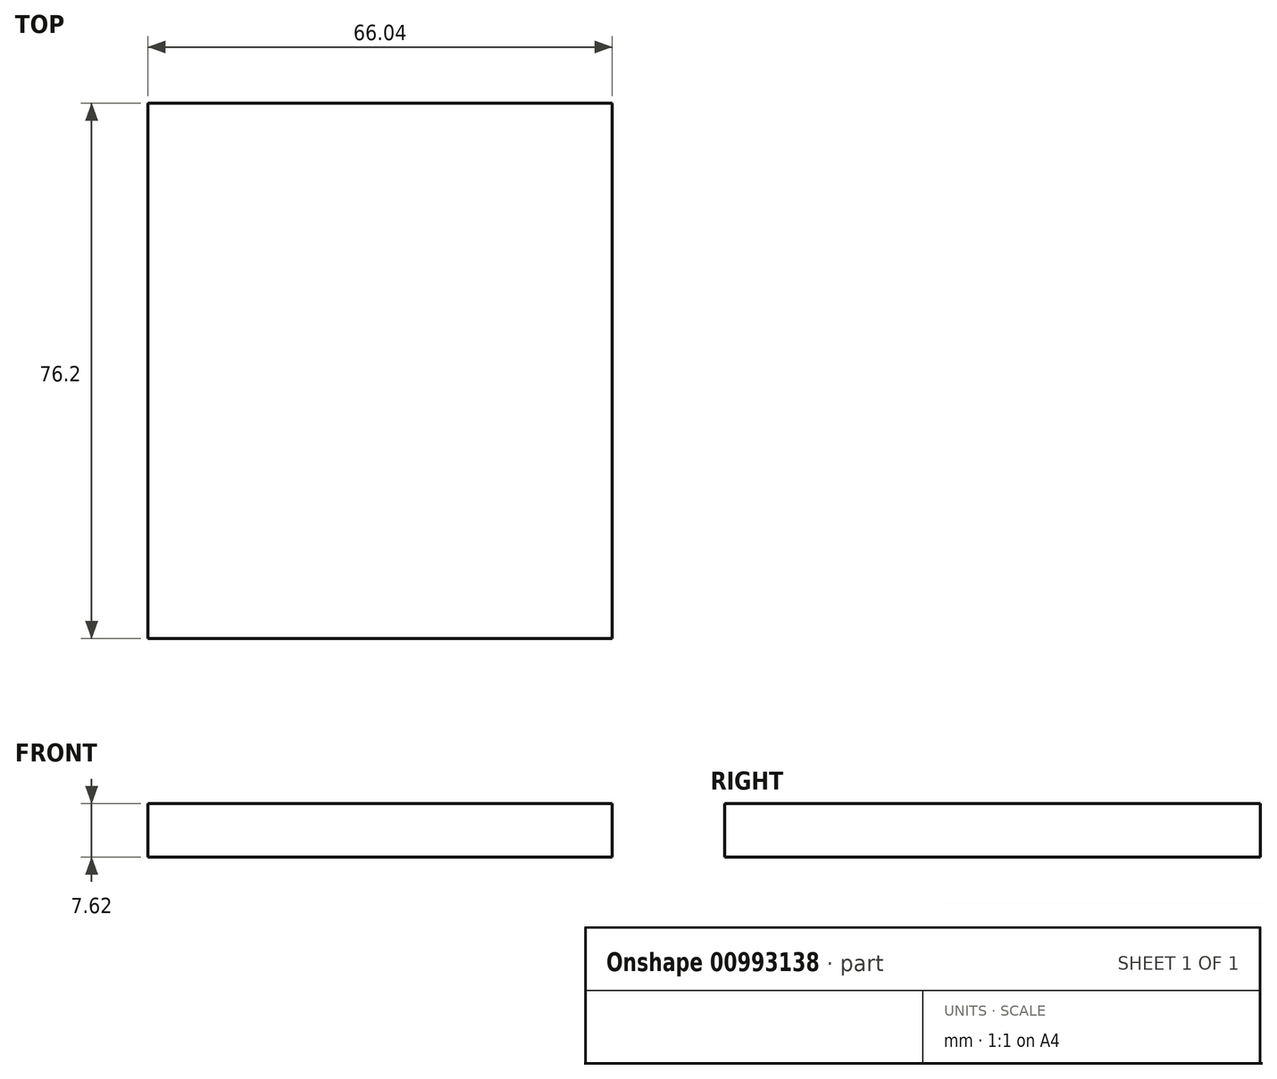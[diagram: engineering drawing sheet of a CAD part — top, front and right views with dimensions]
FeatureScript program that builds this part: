
annotation { "Feature Type Name" : "Feature", "Feature Type Description" : "" }
export const myFeature = defineFeature(function(context is Context, id is Id, definition is map)
    precondition{}
    {
        {
            var Q0;
            Q0=qCreatedBy(makeId("Top.planeOp"),FACE);
            var sketch = newSketch(context, id + "F0", { "sketchPlane" : qUnion([Q0])});
            skLineSegment(sketch, "E0.bottom", {"start": v(-56.06, -63.95) * mm, "end": v(9.98, -63.95) * mm});
            skLineSegment(sketch, "E0.top", {"start": v(-56.06, 12.25) * mm, "end": v(9.98, 12.25) * mm});
            skLineSegment(sketch, "E0.left", {"start": v(-56.06, -63.95) * mm, "end": v(-56.06, 12.25) * mm});
            skLineSegment(sketch, "E0.right", {"start": v(9.98, -63.95) * mm, "end": v(9.98, 12.25) * mm});
            skSolve(sketch);
        }
        {
            var Q0;
            Q0=makeQuery(id+"F0.imprint","IMPRINT",FACE,{"disambiguationData":[TD([[makeQuery(id+"F0.imprint","IMPRINT",EDGE,{"derivedFrom":sQuery(id+"F0.wireOp",EDGE,"E0.bottom")}),1.0]])]});
            extrude(context, id + "F1", {"entities" : qUnion([Q0]), "depth" : 7.62 * mm, "offsetDistance" : 25.4 * mm});
        }
    });
